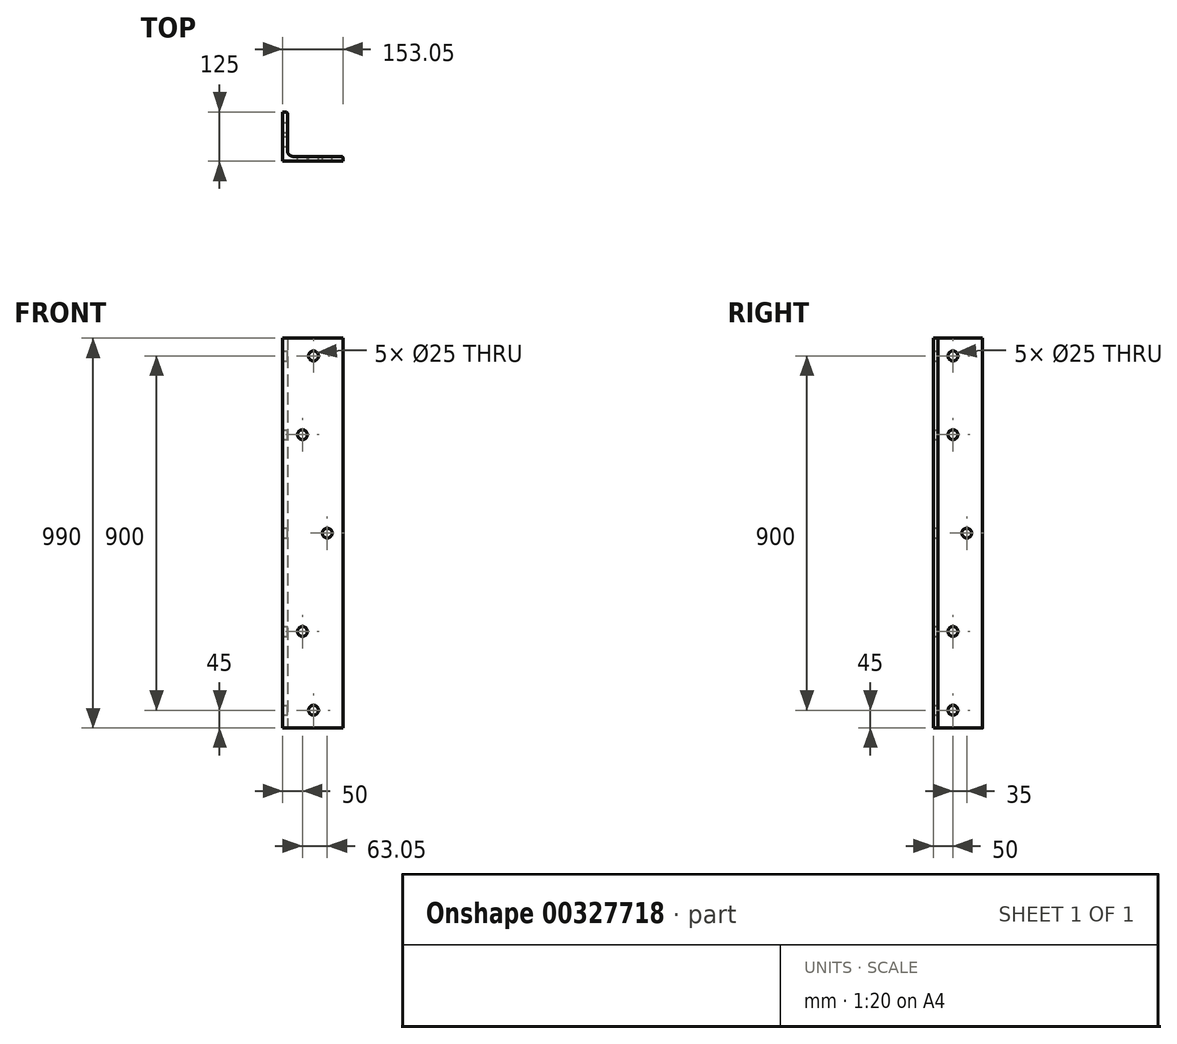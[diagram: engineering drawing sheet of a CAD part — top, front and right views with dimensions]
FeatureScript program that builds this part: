
annotation { "Feature Type Name" : "Feature", "Feature Type Description" : "" }
export const myFeature = defineFeature(function(context is Context, id is Id, definition is map)
    precondition{}
    {
        {
            var Q0;
            Q0=qCreatedBy(makeId("Top.planeOp"),FACE);
            var sketch = newSketch(context, id + "F0", { "sketchPlane" : qUnion([Q0])});
            skLineSegment(sketch, "E0", {"start": v(0, 0) * mm, "end": v(153.05, 0) * mm});
            skLineSegment(sketch, "E1", {"start": v(153.05, 0) * mm, "end": v(153.05, 12) * mm});
            skLineSegment(sketch, "E2", {"start": v(0, 125) * mm, "end": v(12, 125) * mm});
            skLineSegment(sketch, "E3", {"start": v(0, 0) * mm, "end": v(0, 125) * mm});
            skLineSegment(sketch, "E4", {"start": v(12, 125) * mm, "end": v(12, 12) * mm});
            skLineSegment(sketch, "E5", {"start": v(12, 12) * mm, "end": v(153.05, 12) * mm});
            skSolve(sketch);
        }
        {
            var Q0;
            Q0=makeQuery(id+"F0.imprint","IMPRINT",FACE,{"disambiguationData":[TD([[makeQuery(id+"F0.imprint","IMPRINT",EDGE,{"derivedFrom":sQuery(id+"F0.wireOp",EDGE,"E0")}),1.0]])]});
            extrude(context, id + "F1", {"entities" : qUnion([Q0]), "depth" : 990 * mm});
        }
        {
            var Q0;
            Q0=makeQuery(id+"F1.opExtrude","SWEPT_EDGE",EDGE,{"disambiguationData":[OSD([sQuery(id+"F0.wireOp",EDGE,"E4"),sQuery(id+"F0.wireOp",EDGE,"E5")])]});
            fillet(context, id + "F2", {"entities" : qUnion([Q0]), "radius" : 14 * mm, "tangentPropagation" : true, "allowEdgeOverflow" : false});
        }
        {
            var Q0;
            Q0=makeQuery(id+"F1.opExtrude","SWEPT_EDGE",EDGE,{"disambiguationData":[OSD([sQuery(id+"F0.wireOp",EDGE,"E2"),sQuery(id+"F0.wireOp",EDGE,"E4")])]});
            var Q1;
            Q1=makeQuery(id+"F1.opExtrude","SWEPT_EDGE",EDGE,{"disambiguationData":[OSD([sQuery(id+"F0.wireOp",EDGE,"E1"),sQuery(id+"F0.wireOp",EDGE,"E5")])]});
            fillet(context, id + "F3", {"entities" : qUnion([Q0, Q1]), "radius" : 4.6 * mm, "tangentPropagation" : true, "allowEdgeOverflow" : false});
        }
        {
            var Q0;
            Q0=makeQuery(id+"F1.opExtrude","SWEPT_FACE",FACE,{"disambiguationData":[OSD([sQuery(id+"F0.wireOp",EDGE,"E5")])]});
            var sketch = newSketch(context, id + "F4", { "sketchPlane" : qUnion([Q0])});
            skCircle(sketch, "E6", {"center": v(-113.05, 495) * mm, "radius": 12.5 * mm});
            skSolve(sketch);
        }
        {
            var Q0;
            Q0=sQuery(id+"F4.wireOp",VERTEX,"E6.center");
            var Q1;
            Q1=makeQuery(id+"F1.opExtrude","SWEPT_BODY",BODY,{"disambiguationData":[OSD([sQuery(id+"F0.wireOp",EDGE,"E0"),sQuery(id+"F0.wireOp",EDGE,"E1"),sQuery(id+"F0.wireOp",EDGE,"E2"),sQuery(id+"F0.wireOp",EDGE,"E3"),sQuery(id+"F0.wireOp",EDGE,"E4"),sQuery(id+"F0.wireOp",EDGE,"E5")])]});
            hole(context, id + "F5", {"style" : HoleStyle.SIMPLE, "endStyle" : HoleEndStyle.THROUGH, "holeDiameter" : 25 * mm, "tappedDepth" : 12 * mm, "tapClearance" : 3, "locations" : qUnion([Q0]), "scope" : qUnion([Q1])});
        }
        {
            var Q0;
            Q0=makeQuery(id+"F1.opExtrude","SWEPT_FACE",FACE,{"disambiguationData":[OSD([sQuery(id+"F0.wireOp",EDGE,"E5")])]});
            var sketch = newSketch(context, id + "F6", { "sketchPlane" : qUnion([Q0])});
            skCircle(sketch, "E7", {"center": v(-50, 745) * mm, "radius": 12.5 * mm});
            skCircle(sketch, "E8", {"center": v(-78.05, 945) * mm, "radius": 12.5 * mm});
            skCircle(sketch, "E9", {"center": v(-50, 245) * mm, "radius": 12.5 * mm});
            skCircle(sketch, "E10", {"center": v(-78.05, 45) * mm, "radius": 12.5 * mm});
            skSolve(sketch);
        }
        {
            var Q0;
            Q0=sQuery(id+"F6.wireOp",VERTEX,"E8.center");
            var Q1;
            Q1=sQuery(id+"F6.wireOp",VERTEX,"E7.center");
            var Q2;
            Q2=sQuery(id+"F6.wireOp",VERTEX,"E9.center");
            var Q3;
            Q3=sQuery(id+"F6.wireOp",VERTEX,"E10.center");
            var Q4;
            Q4=makeQuery(id+"F1.opExtrude","SWEPT_BODY",BODY,{"disambiguationData":[OSD([sQuery(id+"F0.wireOp",EDGE,"E0"),sQuery(id+"F0.wireOp",EDGE,"E1"),sQuery(id+"F0.wireOp",EDGE,"E2"),sQuery(id+"F0.wireOp",EDGE,"E3"),sQuery(id+"F0.wireOp",EDGE,"E4"),sQuery(id+"F0.wireOp",EDGE,"E5")])]});
            hole(context, id + "F7", {"style" : HoleStyle.SIMPLE, "endStyle" : HoleEndStyle.THROUGH, "holeDiameter" : 25 * mm, "tappedDepth" : 12 * mm, "tapClearance" : 3, "locations" : qUnion([Q0, Q1, Q2, Q3]), "scope" : qUnion([Q4])});
        }
        {
            var Q0;
            Q0=makeQuery(id+"F1.opExtrude","SWEPT_FACE",FACE,{"disambiguationData":[OSD([sQuery(id+"F0.wireOp",EDGE,"E4")])]});
            var sketch = newSketch(context, id + "F8", { "sketchPlane" : qUnion([Q0])});
            skCircle(sketch, "E11", {"center": v(85, 495) * mm, "radius": 12.5 * mm});
            skCircle(sketch, "E12", {"center": v(50, 745) * mm, "radius": 12.5 * mm});
            skCircle(sketch, "E13", {"center": v(50, 945) * mm, "radius": 12.5 * mm});
            skCircle(sketch, "E14", {"center": v(50, 245) * mm, "radius": 12.5 * mm});
            skCircle(sketch, "E15", {"center": v(50, 45) * mm, "radius": 12.5 * mm});
            skSolve(sketch);
        }
        {
            var Q0;
            Q0=sQuery(id+"F8.wireOp",VERTEX,"E13.center");
            var Q1;
            Q1=sQuery(id+"F8.wireOp",VERTEX,"E12.center");
            var Q2;
            Q2=sQuery(id+"F8.wireOp",VERTEX,"E11.center");
            var Q3;
            Q3=sQuery(id+"F8.wireOp",VERTEX,"E14.center");
            var Q4;
            Q4=sQuery(id+"F8.wireOp",VERTEX,"E15.center");
            var Q5;
            Q5=makeQuery(id+"F1.opExtrude","SWEPT_BODY",BODY,{"disambiguationData":[OSD([sQuery(id+"F0.wireOp",EDGE,"E0"),sQuery(id+"F0.wireOp",EDGE,"E1"),sQuery(id+"F0.wireOp",EDGE,"E2"),sQuery(id+"F0.wireOp",EDGE,"E3"),sQuery(id+"F0.wireOp",EDGE,"E4"),sQuery(id+"F0.wireOp",EDGE,"E5")])]});
            hole(context, id + "F9", {"style" : HoleStyle.SIMPLE, "endStyle" : HoleEndStyle.THROUGH, "holeDiameter" : 25 * mm, "tappedDepth" : 12 * mm, "tapClearance" : 3, "locations" : qUnion([Q0, Q1, Q2, Q3, Q4]), "scope" : qUnion([Q5])});
        }
    });
